# Revit family: VTp707 Соединитель под ключ с переходом на НР
name_source: partatom
category: Соединительные детали трубопроводов
revit_build: Autodesk Revit 2015 (Build: 20140606_1530(x64)
units: mm (PartAtom-declared; Revit-internal decimal feet)

## types (7) — shared parameters
Группа модели = VTp.700
Изготовитель = VALTEC S.R.L.
Коэффициент K = 0.5
Метод определения потерь = Коэффициент K
Описание = Соединитель под ключ с переходом на наружн. резьбу
Таблица коэффициентов K = Angle Valve Threaded

## per-type parameters (varying)
| type | 32х1" | 40x1 1/4" | 40x1" | 50x1 1/2" | 63x2" | 75x2 1/2" | 90x3" | A | B | G | Lrez | d | Код по классификатору |
| 32х1" | Да | Нет | Нет | Нет | Нет | Нет | Нет | 71 мм | 19 мм | 25 мм | 13 мм | 32 мм | VTp.707.0.03206 |
| 40x1 1/4" | Нет | Да | Нет | Нет | Нет | Нет | Нет | 80 мм | 21 мм | 32 мм | 14 мм | 40 мм | VTp.707.0.04007 |
| 40x1" | Нет | Нет | Да | Нет | Нет | Нет | Нет | 76 мм | 21 мм | 25 мм | 13 мм | 40 мм | VTp.707.0.04006 |
| 50x1 1/2" | Нет | Нет | Нет | Да | Нет | Нет | Нет | 85 мм | 24 мм | 40 мм | 16 мм | 50 мм | VTp.707.0.05008 |
| 63x2" | Нет | Нет | Нет | Нет | Да | Нет | Нет | 104 мм | 26 мм | 50 мм | 17 мм | 63 мм | VTp.707.0.06309 |
| 75x2 1/2" | Нет | Нет | Нет | Нет | Нет | Да | Нет | 126 мм | 30 мм | 63 мм | 21 мм | 75 мм | VTp.707.0.07510 |
| 90x3" | Нет | Нет | Нет | Нет | Нет | Нет | Да | 137 мм | 33 мм | 75 мм | 22 мм | 90 мм | VTp.707.0.09011 |
